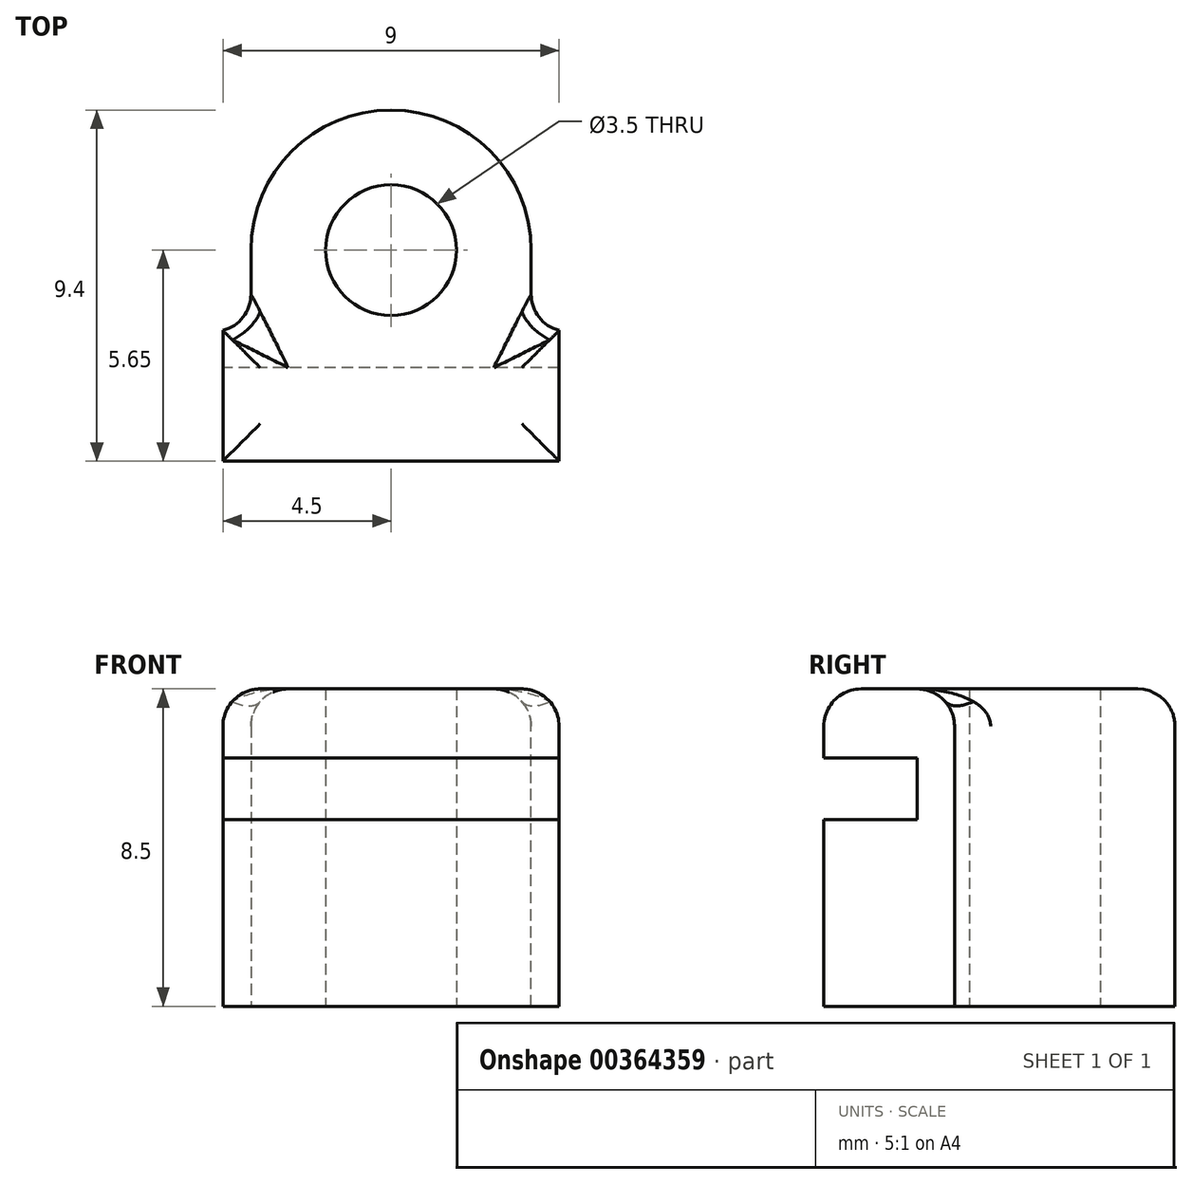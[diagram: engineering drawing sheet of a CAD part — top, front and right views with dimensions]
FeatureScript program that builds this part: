
annotation { "Feature Type Name" : "Feature", "Feature Type Description" : "" }
export const myFeature = defineFeature(function(context is Context, id is Id, definition is map)
    precondition{}
    {
        {
            var Q0;
            Q0=qCreatedBy(makeId("Top.planeOp"),FACE);
            var sketch = newSketch(context, id + "F0", { "sketchPlane" : qUnion([Q0])});
            skCircle(sketch, "E0", {"center": v(0, -1.6) * mm, "radius": 1.75 * mm});
            skCircle(sketch, "E1", {"center": v(0, -1.6) * mm, "radius": 3.75 * mm});
            skLineSegment(sketch, "E2.bottom", {"start": v(0, -3.75) * mm, "end": v(4.5, -3.75) * mm});
            skLineSegment(sketch, "E2.top", {"start": v(0, -7.25) * mm, "end": v(4.5, -7.25) * mm});
            skLineSegment(sketch, "E2.left", {"start": v(0, -3.75) * mm, "end": v(0, -7.25) * mm});
            skLineSegment(sketch, "E2.right", {"start": v(4.5, -3.75) * mm, "end": v(4.5, -7.25) * mm});
            skLineSegment(sketch, "E3.bottom", {"start": v(0, -3.75) * mm, "end": v(-4.5, -3.75) * mm});
            skLineSegment(sketch, "E3.top", {"start": v(0, -7.25) * mm, "end": v(-4.5, -7.25) * mm});
            skLineSegment(sketch, "E3.right", {"start": v(-4.5, -3.75) * mm, "end": v(-4.5, -7.25) * mm});
            skLineSegment(sketch, "E4", {"start": v(3.75, -1.6) * mm, "end": v(3.75, -3.75) * mm});
            skLineSegment(sketch, "E5", {"start": v(-3.75, -1.6) * mm, "end": v(-3.75, -3.75) * mm});
            skSolve(sketch);
        }
        {
            var Q0;
            Q0=makeQuery(id+"F0.imprint","IMPRINT",FACE,{"disambiguationData":[TD([[makeQuery(id+"F0.imprint","IMPRINT",EDGE,{"derivedFrom":sQuery(id+"F0.wireOp",EDGE,"E0")}),-1.0]])]});
            var Q1;
            {var subQ3=sQuery(id+"F0.wireOp",EDGE,"q71p4VKd-kKVK-m9ip-oZHS-NglMbc35WvOL");Q1=makeQuery(id+"F0.imprint","IMPRINT",FACE,{"disambiguationData":[TD([[makeQuery(id+"F0.imprint","IMPRINT",EDGE,{"derivedFrom":subQ3}),1.0]])]});}
            var Q2;
            {var subQ3=sQuery(id+"F0.wireOp",EDGE,"6Fhewj39-U5J2-48Js-fpIo-XNoqiXdD1se0");Q2=makeQuery(id+"F0.imprint","IMPRINT",FACE,{"disambiguationData":[TD([[makeQuery(id+"F0.imprint","IMPRINT",EDGE,{"derivedFrom":subQ3}),-1.0]])]});}
            var Q3;
            Q3=makeQuery(id+"F0.imprint","IMPRINT",FACE,{"disambiguationData":[TD([[makeQuery(id+"F0.imprint","IMPRINT",EDGE,{"derivedFrom":sQuery(id+"F0.wireOp",EDGE,"E2.top")}),1.0]])]});
            var Q4;
            Q4=makeQuery(id+"F0.imprint","IMPRINT",FACE,{"disambiguationData":[TD([[makeQuery(id+"F0.imprint","IMPRINT",EDGE,{"derivedFrom":sQuery(id+"F0.wireOp",EDGE,"E3.top")}),-1.0]])]});
            var Q5;
            {var subQ0=sQuery(id+"F0.wireOp",EDGE,"E3.bottom");var subQ1=sQuery(id+"F0.wireOp",EDGE,"E1");var subQ2=makeQuery(id+"F0.imprint","INTERSECT",VERTEX,{"derivedFrom":[subQ1,subQ0]});Q5=makeQuery(id+"F0.imprint","IMPRINT",FACE,{"disambiguationData":[TD([[makeQuery(id+"F0.imprint","IMPRINT",EDGE,{"disambiguationData":[TD([[subQ2,-1.0]])],"derivedFrom":subQ1}),1.0]])]});}
            var Q6;
            {var subQ0=sQuery(id+"F0.wireOp",EDGE,"E2.left");var subQ1=sQuery(id+"F0.wireOp",EDGE,"E1");var subQ2=makeQuery(id+"F0.imprint","INTERSECT",VERTEX,{"derivedFrom":[subQ1,subQ0]});Q6=makeQuery(id+"F0.imprint","IMPRINT",FACE,{"disambiguationData":[TD([[makeQuery(id+"F0.imprint","IMPRINT",EDGE,{"disambiguationData":[TD([[subQ2,-1.0]])],"derivedFrom":subQ1}),1.0]])]});}
            var Q7;
            {var subQ0=sQuery(id+"F0.wireOp",EDGE,"E4");Q7=makeQuery(id+"F0.imprint","IMPRINT",FACE,{"disambiguationData":[TD([[makeQuery(id+"F0.imprint","IMPRINT",EDGE,{"derivedFrom":subQ0}),-1.0]])]});}
            var Q8;
            {var subQ0=sQuery(id+"F0.wireOp",EDGE,"E5");Q8=makeQuery(id+"F0.imprint","IMPRINT",FACE,{"disambiguationData":[TD([[makeQuery(id+"F0.imprint","IMPRINT",EDGE,{"derivedFrom":subQ0}),1.0]])]});}
            extrude(context, id + "F1", {"entities" : qUnion([Q0, Q1, Q2, Q3, Q4, Q5, Q6, Q7, Q8]), "depth" : 8.5 * mm});
        }
        {
            var Q0;
            Q0=makeQuery(id+"F1.opExtrude","SWEPT_FACE",FACE,{"disambiguationData":[OSD([sQuery(id+"F0.wireOp",EDGE,"E3.right")])]});
            var sketch = newSketch(context, id + "F2", { "sketchPlane" : qUnion([Q0])});
            skLineSegment(sketch, "E6.bottom", {"start": v(7.25, 6.65) * mm, "end": v(4.75, 6.65) * mm});
            skLineSegment(sketch, "E6.top", {"start": v(7.25, 5) * mm, "end": v(4.75, 5) * mm});
            skLineSegment(sketch, "E6.left", {"start": v(7.25, 6.65) * mm, "end": v(7.25, 5) * mm});
            skLineSegment(sketch, "E6.right", {"start": v(4.75, 6.65) * mm, "end": v(4.75, 5) * mm});
            skLineSegment(sketch, "E7", {"start": v(7.25, 5) * mm, "end": v(7.25, 0) * mm});
            skSolve(sketch);
        }
        {
            var Q0;
            Q0=makeQuery(id+"F2.imprint","IMPRINT",FACE,{"disambiguationData":[TD([[makeQuery(id+"F2.imprint","IMPRINT",EDGE,{"derivedFrom":sQuery(id+"F2.wireOp",EDGE,"E6.bottom")}),1.0]])]});
            extrude(context, id + "F3", {"entities" : qUnion([Q0]), "operationType" : NewBodyOperationType.REMOVE, "endBound" : BoundingType.UP_TO_NEXT, "oppositeDirection" : true, "depth" : 25 * mm});
        }
        {
            var Q0;
            Q0=makeQuery(id+"F1.opExtrude","CAP_EDGE",EDGE,{"disambiguationData":[OSD([sQuery(id+"F0.wireOp",EDGE,"E3.right")])],"isStart":false});
            var Q1;
            Q1=makeQuery(id+"F1.opExtrude","CAP_EDGE",EDGE,{"disambiguationData":[OSD([sQuery(id+"F0.wireOp",EDGE,"q71p4VKd-kKVK-m9ip-oZHS-NglMbc35WvOL")])],"isStart":false});
            var Q2;
            Q2=makeQuery(id+"F1.opExtrude","CAP_EDGE",EDGE,{"disambiguationData":[OSD([sQuery(id+"F0.wireOp",EDGE,"E2.right")])],"isStart":false});
            var Q3;
            Q3=makeQuery(id+"F1.opExtrude","CAP_EDGE",EDGE,{"disambiguationData":[OSD([sQuery(id+"F0.wireOp",EDGE,"E2.top"),sQuery(id+"F0.wireOp",EDGE,"E3.top")])],"isStart":false});
            var Q4;
            Q4=makeQuery(id+"F1.opExtrude","CAP_EDGE",EDGE,{"disambiguationData":[OSD([sQuery(id+"F0.wireOp",EDGE,"E1")])],"isStart":false});
            var Q5;
            Q5=makeQuery(id+"F1.opExtrude","CAP_EDGE",EDGE,{"disambiguationData":[OSD([sQuery(id+"F0.wireOp",EDGE,"E5")])],"isStart":false});
            var Q6;
            Q6=makeQuery(id+"F1.opExtrude","CAP_EDGE",EDGE,{"disambiguationData":[OSD([sQuery(id+"F0.wireOp",EDGE,"E3.bottom")])],"isStart":false});
            var Q7;
            Q7=makeQuery(id+"F1.opExtrude","CAP_EDGE",EDGE,{"disambiguationData":[OSD([sQuery(id+"F0.wireOp",EDGE,"E4")])],"isStart":false});
            var Q8;
            Q8=makeQuery(id+"F1.opExtrude","CAP_EDGE",EDGE,{"disambiguationData":[OSD([sQuery(id+"F0.wireOp",EDGE,"E2.bottom")])],"isStart":false});
            fillet(context, id + "F4", {"entities" : qUnion([Q0, Q1, Q2, Q3, Q4, Q5, Q6, Q7, Q8]), "radius" : 1 * mm, "allowEdgeOverflow" : false});
        }
        {
            var Q0;
            Q0=makeQuery(id+"F1.opExtrude","SWEPT_EDGE",EDGE,{"disambiguationData":[OSD([sQuery(id+"F0.wireOp",EDGE,"E2.bottom"),sQuery(id+"F0.wireOp",EDGE,"E4")])]});
            var Q1;
            Q1=makeQuery(id+"F1.opExtrude","SWEPT_EDGE",EDGE,{"disambiguationData":[OSD([sQuery(id+"F0.wireOp",EDGE,"E3.bottom"),sQuery(id+"F0.wireOp",EDGE,"E5")])]});
            var Q2;
            Q2=makeQuery(id+"F4.opFillet","BLEND_EDGE",EDGE,{"blendedFrom":[makeQuery(id+"F1.opExtrude","CAP_EDGE",EDGE,{"disambiguationData":[OSD([sQuery(id+"F0.wireOp",EDGE,"E3.bottom")])],"isStart":false}),makeQuery(id+"F1.opExtrude","CAP_EDGE",EDGE,{"disambiguationData":[OSD([sQuery(id+"F0.wireOp",EDGE,"E5")])],"isStart":false})],"blendedInto":[]});
            var Q3;
            Q3=makeQuery(id+"F4.opFillet","BLEND_EDGE",EDGE,{"blendedFrom":[makeQuery(id+"F1.opExtrude","CAP_EDGE",EDGE,{"disambiguationData":[OSD([sQuery(id+"F0.wireOp",EDGE,"E2.bottom")])],"isStart":false}),makeQuery(id+"F1.opExtrude","CAP_EDGE",EDGE,{"disambiguationData":[OSD([sQuery(id+"F0.wireOp",EDGE,"E4")])],"isStart":false})],"blendedInto":[]});
            fillet(context, id + "F5", {"entities" : qUnion([Q0, Q1, Q2, Q3]), "radius" : 1 * mm, "allowEdgeOverflow" : false});
        }
    });
